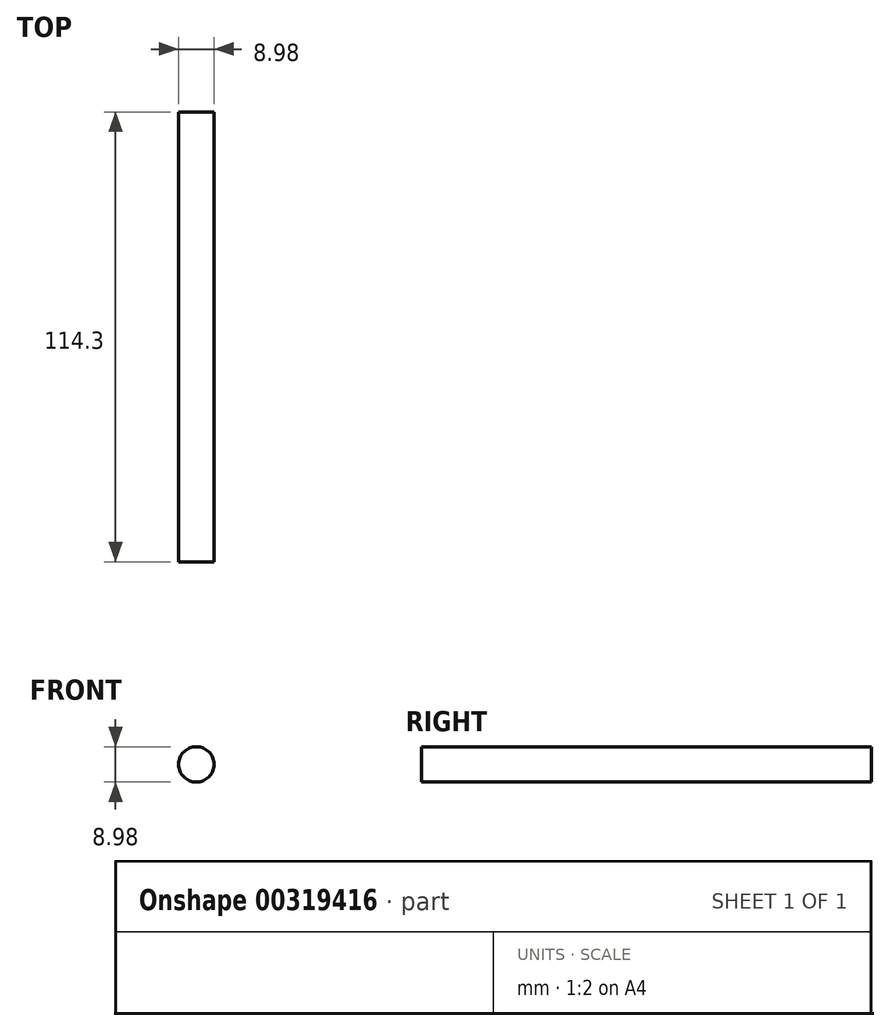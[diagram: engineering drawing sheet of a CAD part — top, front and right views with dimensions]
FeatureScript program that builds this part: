
annotation { "Feature Type Name" : "Feature", "Feature Type Description" : "" }
export const myFeature = defineFeature(function(context is Context, id is Id, definition is map)
    precondition{}
    {
        {
            var Q0;
            Q0=qCreatedBy(makeId("Front.planeOp"),FACE);
            var sketch = newSketch(context, id + "F0", { "sketchPlane" : qUnion([Q0])});
            skCircle(sketch, "E0", {"center": v(0, 0) * mm, "radius": 4.49 * mm});
            skSolve(sketch);
        }
        {
            var Q0;
            Q0 = qSketchRegion(id + "F0", true);
            extrude(context, id + "F1", {"entities" : qUnion([Q0]), "depth" : 114.3 * mm});
        }
    });
